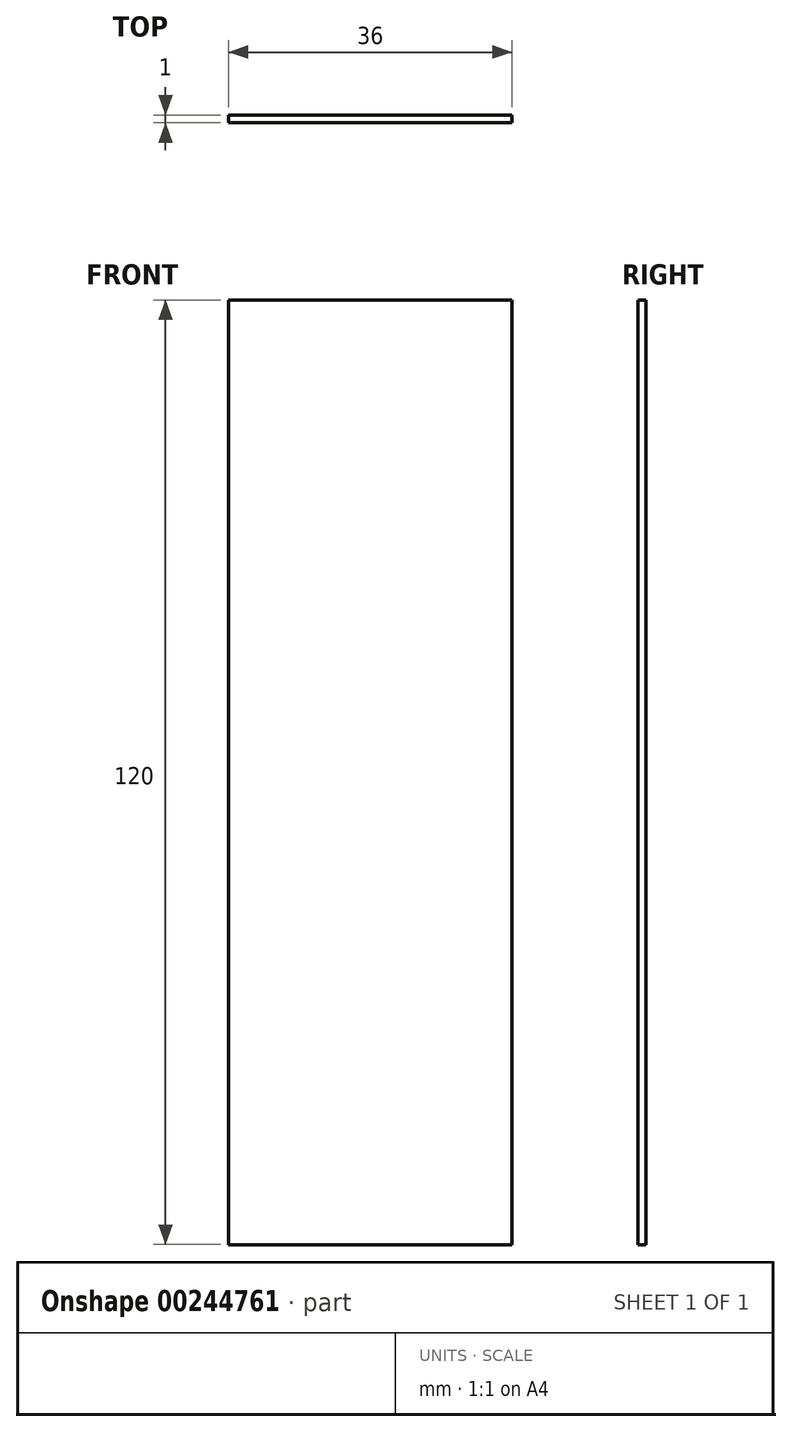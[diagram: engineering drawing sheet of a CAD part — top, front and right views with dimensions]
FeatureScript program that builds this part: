
annotation { "Feature Type Name" : "Feature", "Feature Type Description" : "" }
export const myFeature = defineFeature(function(context is Context, id is Id, definition is map)
    precondition{}
    {
        {
            var Q0;
            Q0=qCreatedBy(makeId("Front.planeOp"),FACE);
            var sketch = newSketch(context, id + "F0", { "sketchPlane" : qUnion([Q0])});
            skLineSegment(sketch, "E0.bottom", {"start": v(24.41, 60.9) * mm, "end": v(60.41, 60.9) * mm});
            skLineSegment(sketch, "E0.top", {"start": v(24.41, -59.1) * mm, "end": v(60.41, -59.1) * mm});
            skLineSegment(sketch, "E0.left", {"start": v(24.41, 60.9) * mm, "end": v(24.41, -59.1) * mm});
            skLineSegment(sketch, "E0.right", {"start": v(60.41, 60.9) * mm, "end": v(60.41, -59.1) * mm});
            skSolve(sketch);
        }
        {
            var Q0;
            Q0=makeQuery(id+"F0.imprint","IMPRINT",FACE,{"disambiguationData":[TD([[makeQuery(id+"F0.imprint","IMPRINT",EDGE,{"derivedFrom":sQuery(id+"F0.wireOp",EDGE,"E0.bottom")}),-1.0]])]});
            extrude(context, id + "F1", {"entities" : qUnion([Q0]), "depth" : 1 * mm});
        }
    });
